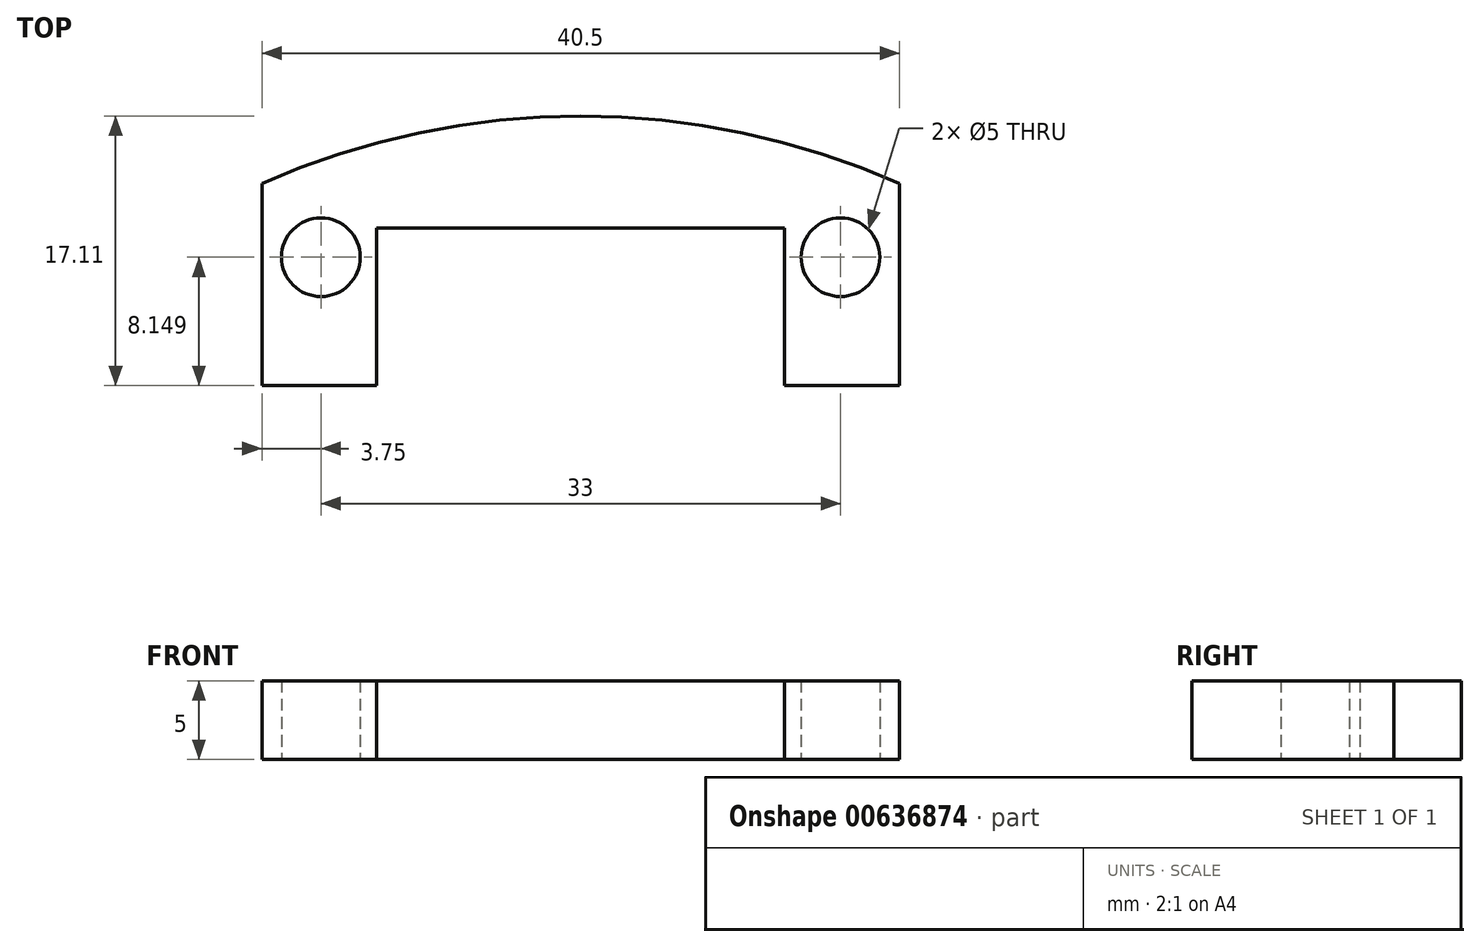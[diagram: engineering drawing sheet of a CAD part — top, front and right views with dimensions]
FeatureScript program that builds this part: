
annotation { "Feature Type Name" : "Feature", "Feature Type Description" : "" }
export const myFeature = defineFeature(function(context is Context, id is Id, definition is map)
    precondition{}
    {
        {
            var Q0;
            Q0=qCreatedBy(makeId("Top.planeOp"),FACE);
            var sketch = newSketch(context, id + "F0", { "sketchPlane" : qUnion([Q0])});
            skArc(sketch, "E0", {"start": v(20.25, 45.72) * mm, "mid": v(0, 50) * mm, "end": v(-20.25, 45.72) * mm});
            skLineSegment(sketch, "E1", {"start": v(20.25, 45.72) * mm, "end": v(20.25, 32.89) * mm});
            skLineSegment(sketch, "E2", {"start": v(20.25, 32.89) * mm, "end": v(12.95, 32.89) * mm});
            skLineSegment(sketch, "E3", {"start": v(12.95, 32.89) * mm, "end": v(12.95, 42.89) * mm});
            skLineSegment(sketch, "E4", {"start": v(12.95, 42.89) * mm, "end": v(-12.95, 42.89) * mm});
            skLineSegment(sketch, "E5", {"start": v(-12.95, 42.89) * mm, "end": v(-12.95, 32.89) * mm});
            skLineSegment(sketch, "E6", {"start": v(-12.95, 32.89) * mm, "end": v(-20.25, 32.89) * mm});
            skLineSegment(sketch, "E7", {"start": v(-20.25, 32.89) * mm, "end": v(-20.25, 45.72) * mm});
            skCircle(sketch, "E8", {"center": v(16.5, 41.04) * mm, "radius": 2.5 * mm});
            skCircle(sketch, "E9.MirrorC", {"center": v(-16.5, 41.04) * mm, "radius": 2.5 * mm});
            skSolve(sketch);
        }
        {
            var Q0;
            Q0 = qSketchRegion(id + "F0", true);
            var Q1;
            Q1=makeQuery(id+"F0.imprint","IMPRINT",FACE,{"disambiguationData":[TD([[makeQuery(id+"F0.imprint","IMPRINT",EDGE,{"derivedFrom":sQuery(id+"F0.wireOp",EDGE,"E0")}),1.0]])]});
            extrude(context, id + "F1", {"entities" : qUnion([Q0, Q1]), "depth" : 5 * mm, "offsetDistance" : 25 * mm});
        }
    });
